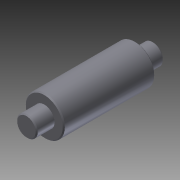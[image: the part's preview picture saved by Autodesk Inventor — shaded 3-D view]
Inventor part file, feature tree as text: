
AUTODESK INVENTOR PART (.ipt)
format: ipt  version: 2011 (Build 150239000, 239)  size: 96,768 bytes
history: native  units: mm (DEFAULTED — no unit token found)
features: extrude x2, sketch x2, reference x2, mirror x1, chamfer x1
ambient origin geometry x8: Origin, YZ Plane, XZ Plane, XY Plane, X Axis, Y Axis, Z Axis, Center Point
bodies: Solid1 (feature_tree)
feature tree (8):
  extrude  "Extrusion1"  Depth=11.176mm TaperAngle=0.0deg
  extrude  "Extrusion2"  Depth=0.127mm
  mirror  "Mirror1"
  chamfer  "Chamfer1"  Angle=45.0deg  [1 undecoded]
  sketch  "Sketch1"  dims[d0=4.7752mm d1=11.176mm d2=0.0mm]
  reference  "Reference1"
  sketch  "Sketch2"  dims[d3=2.1844mm d4=0.0mm d5=0.127mm d6=3.175mm d7=45.0deg]
  reference  "Reference2"
note: 1 required parameter value undecoded (feature->parameter linkage not recoverable at this tier; creation-order binding heuristic only, values carry confidence <= 0.55)
